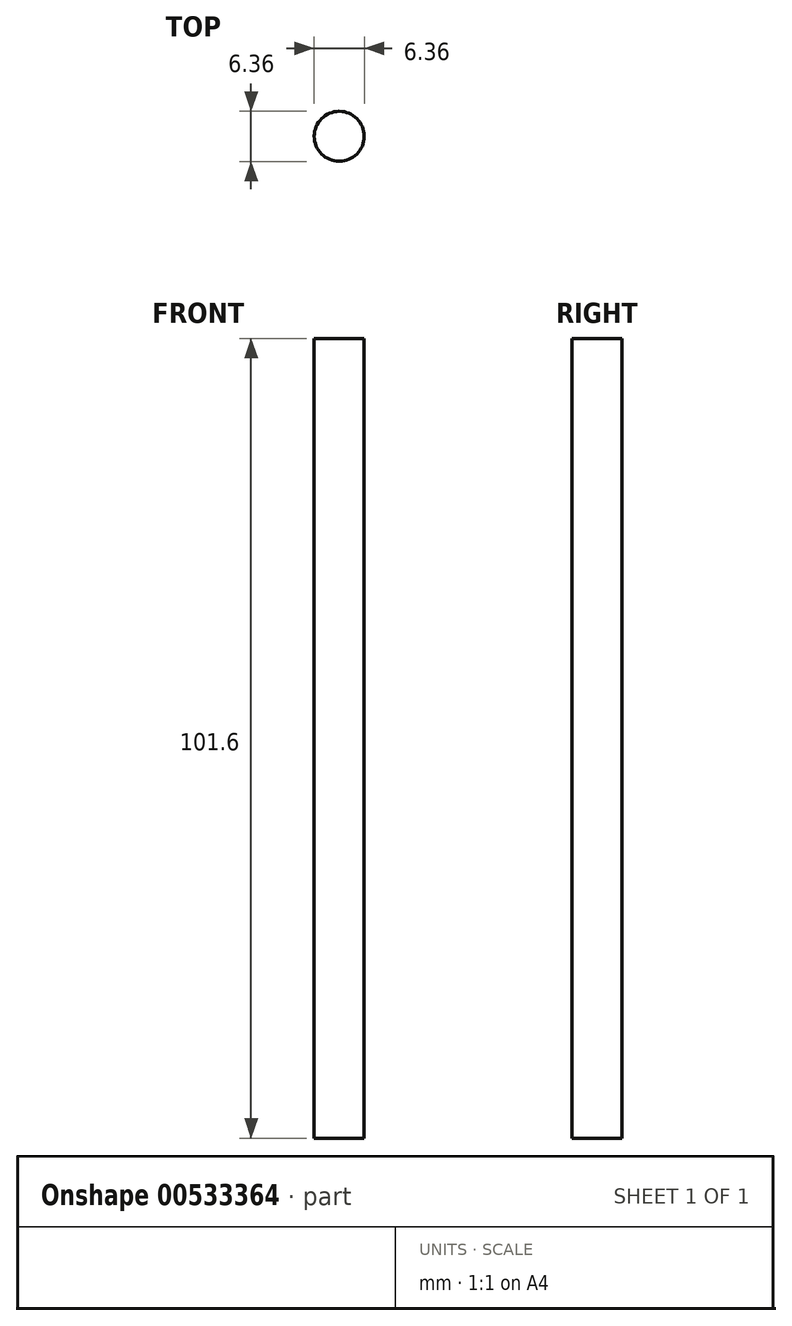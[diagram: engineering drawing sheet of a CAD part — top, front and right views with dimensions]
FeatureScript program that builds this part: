
annotation { "Feature Type Name" : "Feature", "Feature Type Description" : "" }
export const myFeature = defineFeature(function(context is Context, id is Id, definition is map)
    precondition{}
    {
        {
            var Q0;
            Q0=qCreatedBy(makeId("Top.planeOp"),FACE);
            var sketch = newSketch(context, id + "F0", { "sketchPlane" : qUnion([Q0])});
            skCircle(sketch, "E0", {"center": v(0, 0) * mm, "radius": 3.17 * mm});
            skSolve(sketch);
        }
        {
            var Q0;
            Q0 = qSketchRegion(id + "F0", true);
            extrude(context, id + "F1", {"entities" : qUnion([Q0]), "depth" : 101.6 * mm, "offsetDistance" : 25.4 * mm});
        }
    });
